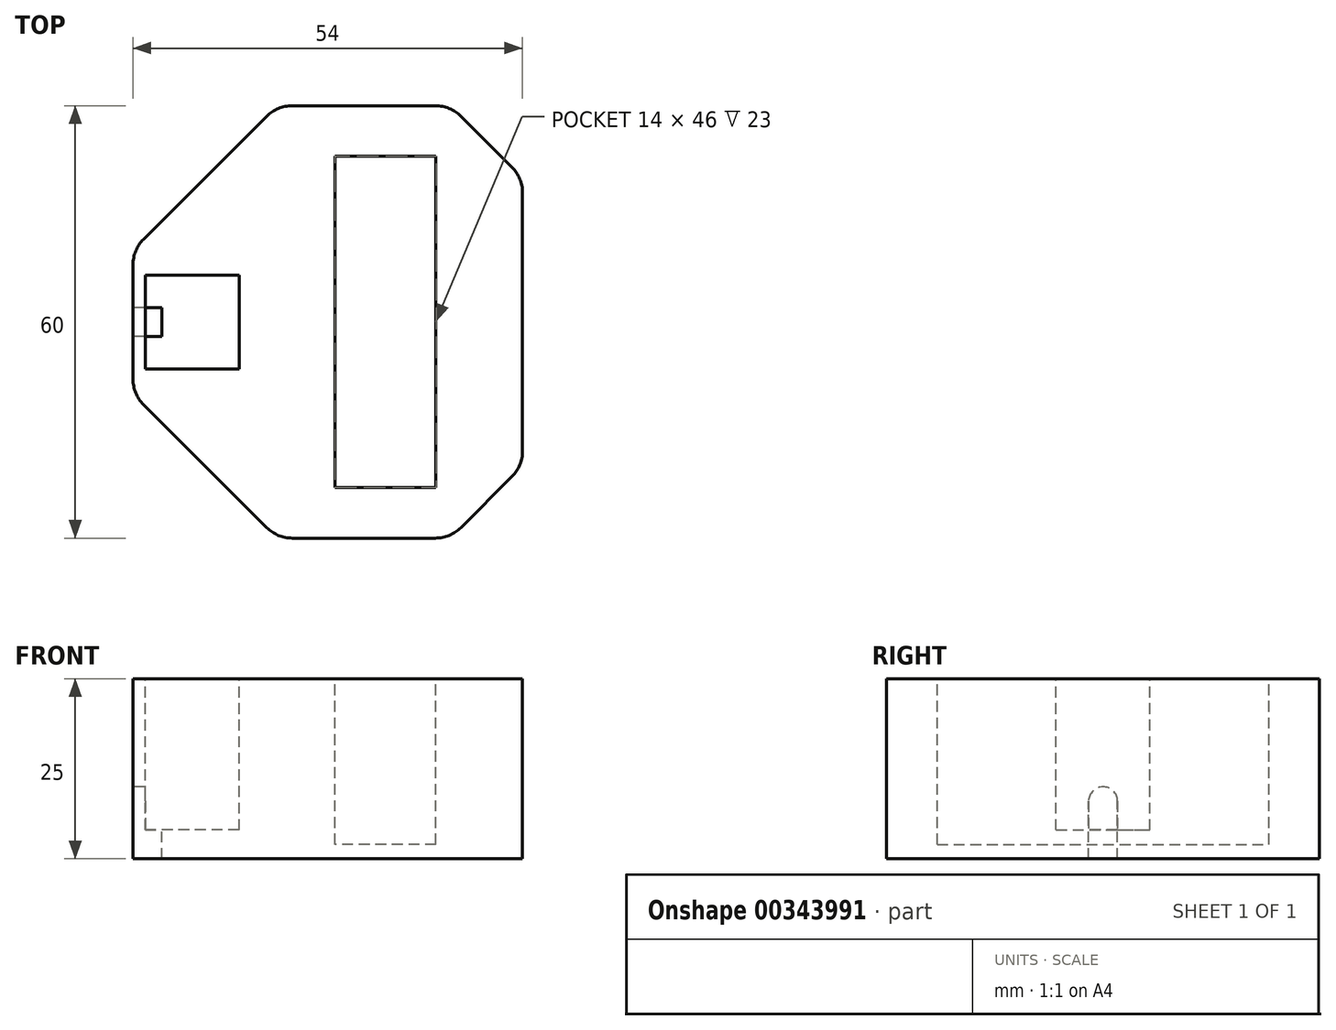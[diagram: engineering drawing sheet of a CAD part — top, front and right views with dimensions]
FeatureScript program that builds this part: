
annotation { "Feature Type Name" : "Feature", "Feature Type Description" : "" }
export const myFeature = defineFeature(function(context is Context, id is Id, definition is map)
    precondition{}
    {
        {
            var Q0;
            Q0=qCreatedBy(makeId("Top.planeOp"),FACE);
            var sketch = newSketch(context, id + "F0", { "sketchPlane" : qUnion([Q0])});
            skLineSegment(sketch, "E0.bottom", {"start": v(35, -30) * mm, "end": v(-35, -30) * mm});
            skLineSegment(sketch, "E0.top", {"start": v(35, 30) * mm, "end": v(-35, 30) * mm});
            skLineSegment(sketch, "E0.left", {"start": v(35, -30) * mm, "end": v(35, 30) * mm});
            skLineSegment(sketch, "E0.right", {"start": v(-35, -30) * mm, "end": v(-35, 30) * mm});
            skPoint(sketch, "E0.middle", {"position": v(0, 0) * mm});
            skLineSegment(sketch, "E1.bottom", {"start": v(7, -23) * mm, "end": v(-7, -23) * mm});
            skLineSegment(sketch, "E1.top", {"start": v(7, 23) * mm, "end": v(-7, 23) * mm});
            skLineSegment(sketch, "E1.left", {"start": v(7, -23) * mm, "end": v(7, 23) * mm});
            skLineSegment(sketch, "E1.right", {"start": v(-7, -23) * mm, "end": v(-7, 23) * mm});
            skCircle(sketch, "E2", {"center": v(0, 0) * mm, "radius": 27.5 * mm, "construction": true});
            skCircle(sketch, "E3.0", {"center": v(0, 0) * mm, "radius": 26.1 * mm, "construction": true});
            skLineSegment(sketch, "E4", {"start": v(-26.1, 0) * mm, "end": v(-27.5, 0) * mm, "construction": true});
            skPoint(sketch, "E5", {"position": v(-26.8, 0) * mm});
            skCircle(sketch, "E6", {"center": v(-26.8, 0) * mm, "radius": 2.5 * mm, "construction": true});
            skLineSegment(sketch, "E7.bottom", {"start": v(-20.3, -6.5) * mm, "end": v(-33.3, -6.5) * mm});
            skLineSegment(sketch, "E7.top", {"start": v(-20.3, 6.5) * mm, "end": v(-33.3, 6.5) * mm});
            skLineSegment(sketch, "E7.left", {"start": v(-20.3, -6.5) * mm, "end": v(-20.3, 6.5) * mm});
            skLineSegment(sketch, "E7.right", {"start": v(-33.3, -6.5) * mm, "end": v(-33.3, 6.5) * mm});
            skLineSegment(sketch, "E8", {"start": v(19, 30) * mm, "end": v(19, -30) * mm});
            skSolve(sketch);
        }
        {
            var Q0;
            {var subQ0=sQuery(id+"F0.wireOp",EDGE,"E0.right");Q0=makeQuery(id+"F0.imprint","IMPRINT",FACE,{"disambiguationData":[TD([[makeQuery(id+"F0.imprint","IMPRINT",EDGE,{"derivedFrom":subQ0}),-1.0]])]});}
            var Q1;
            Q1=makeQuery(id+"F0.imprint","IMPRINT",FACE,{"disambiguationData":[TD([[makeQuery(id+"F0.imprint","IMPRINT",EDGE,{"derivedFrom":sQuery(id+"F0.wireOp",EDGE,"E7.bottom")}),-1.0]])]});
            var Q2;
            Q2=makeQuery(id+"F0.imprint","IMPRINT",FACE,{"disambiguationData":[TD([[makeQuery(id+"F0.imprint","IMPRINT",EDGE,{"derivedFrom":sQuery(id+"F0.wireOp",EDGE,"E1.bottom")}),-1.0]])]});
            extrude(context, id + "F1", {"entities" : qUnion([Q0, Q1, Q2]), "oppositeDirection" : true, "depth" : 25 * mm});
        }
        {
            var Q0;
            Q0=makeQuery(id+"F0.imprint","IMPRINT",FACE,{"disambiguationData":[TD([[makeQuery(id+"F0.imprint","IMPRINT",EDGE,{"derivedFrom":sQuery(id+"F0.wireOp",EDGE,"E7.bottom")}),-1.0]])]});
            extrude(context, id + "F2", {"entities" : qUnion([Q0]), "operationType" : NewBodyOperationType.REMOVE, "oppositeDirection" : true, "depth" : 21 * mm});
        }
        {
            var Q0;
            Q0=makeQuery(id+"F0.imprint","IMPRINT",FACE,{"disambiguationData":[TD([[makeQuery(id+"F0.imprint","IMPRINT",EDGE,{"derivedFrom":sQuery(id+"F0.wireOp",EDGE,"E1.bottom")}),-1.0]])]});
            extrude(context, id + "F3", {"entities" : qUnion([Q0]), "operationType" : NewBodyOperationType.REMOVE, "oppositeDirection" : true, "depth" : 23 * mm});
        }
        {
            var Q0;
            Q0=makeQuery(id+"F1.opExtrude","SWEPT_FACE",FACE,{"disambiguationData":[OSD([sQuery(id+"F0.wireOp",EDGE,"E0.right")])]});
            var sketch = newSketch(context, id + "F4", { "sketchPlane" : qUnion([Q0])});
            skLineSegment(sketch, "E9.0", {"start": v(-6.5, -21) * mm, "end": v(-6.5, 0) * mm, "construction": true});
            skLineSegment(sketch, "E10.0", {"start": v(6.5, -21) * mm, "end": v(-6.5, -21) * mm, "construction": true});
            skLineSegment(sketch, "E11.0", {"start": v(6.5, -21) * mm, "end": v(6.5, 0) * mm, "construction": true});
            skLineSegment(sketch, "E12", {"start": v(-6.5, -21) * mm, "end": v(-6.5, -25) * mm, "construction": true});
            skLineSegment(sketch, "E13", {"start": v(6.5, -21) * mm, "end": v(6.5, -25) * mm, "construction": true});
            skLineSegment(sketch, "E14.bottom", {"start": v(2, -25) * mm, "end": v(-2, -25) * mm});
            skLineSegment(sketch, "E14.top", {"start": v(2, -17) * mm, "end": v(-2, -17) * mm});
            skLineSegment(sketch, "E14.left", {"start": v(2, -25) * mm, "end": v(2, -17) * mm});
            skLineSegment(sketch, "E14.right", {"start": v(-2, -25) * mm, "end": v(-2, -17) * mm});
            skPoint(sketch, "E14.middle", {"position": v(0, -21) * mm});
            skCircle(sketch, "E15", {"center": v(0, -17) * mm, "radius": 2 * mm});
            skSolve(sketch);
        }
        {
            var Q0;
            Q0=makeQuery(id+"F4.imprint","IMPRINT",FACE,{"disambiguationData":[TD([[makeQuery(id+"F4.imprint","IMPRINT",EDGE,{"derivedFrom":sQuery(id+"F4.wireOp",EDGE,"E14.bottom")}),-1.0]])]});
            var Q1;
            {var subQ0=sQuery(id+"F4.wireOp",EDGE,"E14.top");Q1=makeQuery(id+"F4.imprint","IMPRINT",FACE,{"disambiguationData":[TD([[makeQuery(id+"F4.imprint","IMPRINT",EDGE,{"derivedFrom":subQ0}),1.0]])]});}
            var Q2;
            {var subQ0=sQuery(id+"F4.wireOp",EDGE,"E14.top");Q2=makeQuery(id+"F4.imprint","IMPRINT",FACE,{"disambiguationData":[TD([[makeQuery(id+"F4.imprint","IMPRINT",EDGE,{"derivedFrom":subQ0}),-1.0]])]});}
            extrude(context, id + "F5", {"entities" : qUnion([Q0, Q1, Q2]), "operationType" : NewBodyOperationType.REMOVE, "oppositeDirection" : true, "depth" : 4 * mm});
        }
        {
            var Q0;
            Q0=makeQuery(id+"F1.opExtrude","SWEPT_EDGE",EDGE,{"disambiguationData":[OSD([sQuery(id+"F0.wireOp",EDGE,"E0.top"),sQuery(id+"F0.wireOp",EDGE,"E0.right")])]});
            chamfer(context, id + "F6", {"entities" : qUnion([Q0]), "width" : 20 * mm, "tangentPropagation" : true});
        }
        {
            var Q0;
            Q0=makeQuery(id+"F1.opExtrude","SWEPT_EDGE",EDGE,{"disambiguationData":[OSD([sQuery(id+"F0.wireOp",EDGE,"E0.bottom"),sQuery(id+"F0.wireOp",EDGE,"E0.right")])]});
            chamfer(context, id + "F7", {"entities" : qUnion([Q0]), "width" : 20 * mm, "tangentPropagation" : true});
        }
        {
            var Q0;
            Q0=makeQuery(id+"F1.opExtrude","SWEPT_EDGE",EDGE,{"disambiguationData":[OSD([sQuery(id+"F0.wireOp",EDGE,"E0.bottom"),sQuery(id+"F0.wireOp",EDGE,"E8")])]});
            var Q1;
            Q1=makeQuery(id+"F1.opExtrude","SWEPT_EDGE",EDGE,{"disambiguationData":[OSD([sQuery(id+"F0.wireOp",EDGE,"E0.top"),sQuery(id+"F0.wireOp",EDGE,"E8")])]});
            chamfer(context, id + "F8", {"entities" : qUnion([Q0, Q1]), "width" : 10 * mm, "tangentPropagation" : true});
        }
        {
            var Q0;
            {var subQ0=sQuery(id+"F0.wireOp",EDGE,"E0.right");Q0=makeQuery(id+"F6.opChamfer","BLEND_EDGE",EDGE,{"blendedFrom":[makeQuery(id+"F1.opExtrude","SWEPT_EDGE",EDGE,{"disambiguationData":[OSD([sQuery(id+"F0.wireOp",EDGE,"E0.top"),subQ0])]}),makeQuery(id+"F1.opExtrude","SWEPT_FACE",FACE,{"disambiguationData":[OSD([subQ0])]})],"blendedInto":[makeQuery(id+"F1.opExtrude","SWEPT_FACE",FACE,{"disambiguationData":[OSD([subQ0])]})]});}
            var Q1;
            {var subQ0=sQuery(id+"F0.wireOp",EDGE,"E0.right");Q1=makeQuery(id+"F7.opChamfer","BLEND_EDGE",EDGE,{"blendedFrom":[makeQuery(id+"F1.opExtrude","SWEPT_EDGE",EDGE,{"disambiguationData":[OSD([sQuery(id+"F0.wireOp",EDGE,"E0.bottom"),subQ0])]}),makeQuery(id+"F1.opExtrude","SWEPT_FACE",FACE,{"disambiguationData":[OSD([subQ0])]})],"blendedInto":[makeQuery(id+"F1.opExtrude","SWEPT_FACE",FACE,{"disambiguationData":[OSD([subQ0])]})]});}
            var Q2;
            {var subQ0=sQuery(id+"F0.wireOp",EDGE,"E0.bottom");Q2=makeQuery(id+"F7.opChamfer","BLEND_EDGE",EDGE,{"blendedFrom":[makeQuery(id+"F1.opExtrude","SWEPT_EDGE",EDGE,{"disambiguationData":[OSD([subQ0,sQuery(id+"F0.wireOp",EDGE,"E0.right")])]}),makeQuery(id+"F1.opExtrude","SWEPT_FACE",FACE,{"disambiguationData":[OSD([subQ0])]})],"blendedInto":[makeQuery(id+"F1.opExtrude","SWEPT_FACE",FACE,{"disambiguationData":[OSD([subQ0])]})]});}
            var Q3;
            {var subQ0=sQuery(id+"F0.wireOp",EDGE,"E0.bottom");Q3=makeQuery(id+"F8.opChamfer","BLEND_EDGE",EDGE,{"blendedFrom":[makeQuery(id+"F1.opExtrude","SWEPT_EDGE",EDGE,{"disambiguationData":[OSD([subQ0,sQuery(id+"F0.wireOp",EDGE,"E8")])]}),makeQuery(id+"F1.opExtrude","SWEPT_FACE",FACE,{"disambiguationData":[OSD([subQ0])]})],"blendedInto":[makeQuery(id+"F1.opExtrude","SWEPT_FACE",FACE,{"disambiguationData":[OSD([subQ0])]})]});}
            var Q4;
            {var subQ0=sQuery(id+"F0.wireOp",EDGE,"E8");Q4=makeQuery(id+"F8.opChamfer","BLEND_EDGE",EDGE,{"blendedFrom":[makeQuery(id+"F1.opExtrude","SWEPT_EDGE",EDGE,{"disambiguationData":[OSD([sQuery(id+"F0.wireOp",EDGE,"E0.bottom"),subQ0])]}),makeQuery(id+"F1.opExtrude","SWEPT_FACE",FACE,{"disambiguationData":[OSD([subQ0])]})],"blendedInto":[makeQuery(id+"F1.opExtrude","SWEPT_FACE",FACE,{"disambiguationData":[OSD([subQ0])]})]});}
            var Q5;
            {var subQ0=sQuery(id+"F0.wireOp",EDGE,"E8");Q5=makeQuery(id+"F8.opChamfer","BLEND_EDGE",EDGE,{"blendedFrom":[makeQuery(id+"F1.opExtrude","SWEPT_EDGE",EDGE,{"disambiguationData":[OSD([sQuery(id+"F0.wireOp",EDGE,"E0.top"),subQ0])]}),makeQuery(id+"F1.opExtrude","SWEPT_FACE",FACE,{"disambiguationData":[OSD([subQ0])]})],"blendedInto":[makeQuery(id+"F1.opExtrude","SWEPT_FACE",FACE,{"disambiguationData":[OSD([subQ0])]})]});}
            var Q6;
            {var subQ0=sQuery(id+"F0.wireOp",EDGE,"E0.top");Q6=makeQuery(id+"F8.opChamfer","BLEND_EDGE",EDGE,{"blendedFrom":[makeQuery(id+"F1.opExtrude","SWEPT_EDGE",EDGE,{"disambiguationData":[OSD([subQ0,sQuery(id+"F0.wireOp",EDGE,"E8")])]}),makeQuery(id+"F1.opExtrude","SWEPT_FACE",FACE,{"disambiguationData":[OSD([subQ0])]})],"blendedInto":[makeQuery(id+"F1.opExtrude","SWEPT_FACE",FACE,{"disambiguationData":[OSD([subQ0])]})]});}
            var Q7;
            {var subQ0=sQuery(id+"F0.wireOp",EDGE,"E0.top");Q7=makeQuery(id+"F6.opChamfer","BLEND_EDGE",EDGE,{"blendedFrom":[makeQuery(id+"F1.opExtrude","SWEPT_EDGE",EDGE,{"disambiguationData":[OSD([subQ0,sQuery(id+"F0.wireOp",EDGE,"E0.right")])]}),makeQuery(id+"F1.opExtrude","SWEPT_FACE",FACE,{"disambiguationData":[OSD([subQ0])]})],"blendedInto":[makeQuery(id+"F1.opExtrude","SWEPT_FACE",FACE,{"disambiguationData":[OSD([subQ0])]})]});}
            fillet(context, id + "F9", {"entities" : qUnion([Q0, Q1, Q2, Q3, Q4, Q5, Q6, Q7]), "radius" : 5 * mm, "tangentPropagation" : true, "allowEdgeOverflow" : false});
        }
    });
